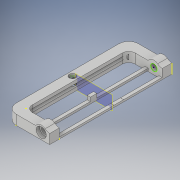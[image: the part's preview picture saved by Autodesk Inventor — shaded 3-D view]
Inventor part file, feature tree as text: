
AUTODESK INVENTOR PART (.ipt)
format: ipt  version: 2018 (Build 220112000, 112)  size: 576,000 bytes
history: native  units: in
note: dims shown in document units (in); Inventor stores cm internally (conversion verified against a paired STEP export)
features: sketch x39, extrude x25, fillet x7, hole x2, plane x1, mirror x1
ambient origin geometry x8: Origin, YZ Plane, XZ Plane, XY Plane, X Axis, Y Axis, Z Axis, Center Point
bodies: Solid1 (feature_tree)
feature tree (75):
  extrude  "Extrusion1"  Depth=0.375in
  sketch  "Sketch2"  dims[d3=0.375in d4=0.5in d5=0.375in d6=0.0in]
  extrude  "Extrusion2"  Depth=0.5in
  fillet  "Fillet1"  Radius=0.375in
  extrude  "Extrusion3"  Depth=0.375in
  extrude  "Extrusion4"  Depth=0.25in
  plane  "Work Plane1"
  mirror  "Mirror1"
  fillet  "Fillet2"  Radius=0.24in
  extrude  "Extrusion5"  Depth=0.375in
  sketch  "Sketch6"  dims[d17=1.0in d18=0.0in d19=0.24in d20=0.0in]
  extrude  "Extrusion6"  Depth=0.24in TaperAngle=0.0deg
  extrude  "Extrusion7"  Depth=0.375in
  fillet  "Fillet3"  Radius=0.25in
  fillet  "Fillet4"  Radius=0.375in
  fillet  "Fillet5"  Radius=0.25in
  fillet  "Fillet6"  Radius=0.125in
  sketch  "Sketch9"  dims[d30=0.125in d31=0.125in]
  extrude  "Extrusion8"  Depth=0.035in
  sketch  "Sketch11"  dims[d35=0.2in]
  sketch  "Sketch12"  dims[d36=0.2in d37=0.75in d38=0.375in d39=0.25in d40=0.5635in d41=0.35in d42=0.0in]
  hole  "Hole1"  [1 undecoded]
  hole  "Hole2"  [1 undecoded]
  sketch  "Sketch14"  dims[d51=3.5in d52=0.375in d53=0.0in]
  extrude  "Extrusion9"  Depth=0.125in
  sketch  "Sketch16"  dims[d58=0.4375in d59=0.0in d60=0.0625in d61=0.0in]
  extrude  "Extrusion10"  Depth=0.375in TaperAngle=0.0deg
  extrude  "Extrusion11"  Depth=0.25in
  extrude  "Extrusion12"  Depth=0.0625in TaperAngle=0.0deg
  sketch  "Sketch20"  dims[d72=0.39in d73=0.135in d74=0.0in]
  sketch  "Sketch21"  dims[d75=0.39in d76=0.135in d77=0.0in]
  sketch  "Sketch22"  dims[d78=0.4475in d79=0.0in d80=0.375in d81=0.0in]
  extrude  "Extrusion13"  Depth=0.125in
  extrude  "Extrusion14"  Depth=0.25in TaperAngle=0.0deg
  fillet  "Fillet7"  Radius=0.25in
  extrude  "Extrusion15"  Depth=0.125in
  extrude  "Extrusion16"  Depth=0.135in TaperAngle=0.0deg
  extrude  "Extrusion17"  Depth=0.135in TaperAngle=0.0deg
  extrude  "Extrusion18"  Depth=0.375in TaperAngle=0.0deg
  sketch  "Sketch29"  dims[d100=0.15in d101=0.0in]
  extrude  "Extrusion19"  Depth=0.375in TaperAngle=0.0deg
  sketch  "Sketch31"
  extrude  "Extrusion20"  Depth=0.375in TaperAngle=0.0deg
  extrude  "Extrusion21"  Depth=0.125in
  sketch  "Sketch34"
  sketch  "Sketch35"
  extrude  "Extrusion22"  Depth=0.375in TaperAngle=0.0deg
  extrude  "Extrusion23"  Depth=0.0425in TaperAngle=0.0deg
  extrude  "Extrusion24"  Depth=0.25in
  extrude  "Extrusion25"  [1 undecoded]
  sketch  "Sketch1"  dims[d0=1.3in d1=0.375in]
  sketch  "Sketch3"  dims[d7=0.375in d8=0.0in d9=0.375in]
  sketch  "Sketch4"  dims[d10=0.24in d11=0.0in d12=0.25in d13=0.24in d14=0.0in]
  sketch  "Sketch5"  dims[d15=2.0in d16=0.375in]
  sketch  "Sketch7"  dims[d21=0.375in d22=0.0in d23=0.375in d24=0.25in d25=0.375in d26=0.25in d27=0.125in]
  sketch  "Sketch8"  dims[d28=0.035in d29=0.035in]
  sketch  "Sketch10"  dims[d32=4.375in d33=0.0in d34=0.2in]
  sketch  "Sketch13"  dims[d43=0.2in d44=0.75in d45=0.375in d46=0.25in d47=0.5635in d48=0.35in d49=0.0in d50=0.125in]
  sketch  "Sketch15"  dims[d56=0.25in d57=0.25in]
  sketch  "Sketch17"  dims[d62=0.04in d63=0.0in d64=0.125in]
  sketch  "Sketch18"  dims[d65=0.075in d66=4.04in d67=0.0in d68=0.25in]
  sketch  "Sketch19"  dims[d69=0.075in d70=0.0in d71=0.125in]
  sketch  "Sketch23"  dims[d82=0.25in d83=0.375in d84=0.0in]
  sketch  "Sketch24"  dims[d85=0.125in d86=0.375in d87=0.0in]
  sketch  "Sketch25"  dims[d88=0.125in d89=0.0in d90=0.125in]
  sketch  "Sketch26"  dims[d91=0.15in d92=0.375in d93=0.0in]
  sketch  "Sketch27"  dims[d94=0.148in d95=0.0in d96=0.0425in d97=0.0in]
  sketch  "Sketch28"  dims[d98=0.125in d99=0.25in]
  sketch  "Sketch30"
  sketch  "Sketch32"
  sketch  "Sketch33"
  sketch  "Sketch36"
  sketch  "Sketch37"
  sketch  "Sketch38"
  sketch  "Sketch39"
note: 3 required parameter values undecoded (feature->parameter linkage not recoverable at this tier; creation-order binding heuristic only, values carry confidence <= 0.55)
